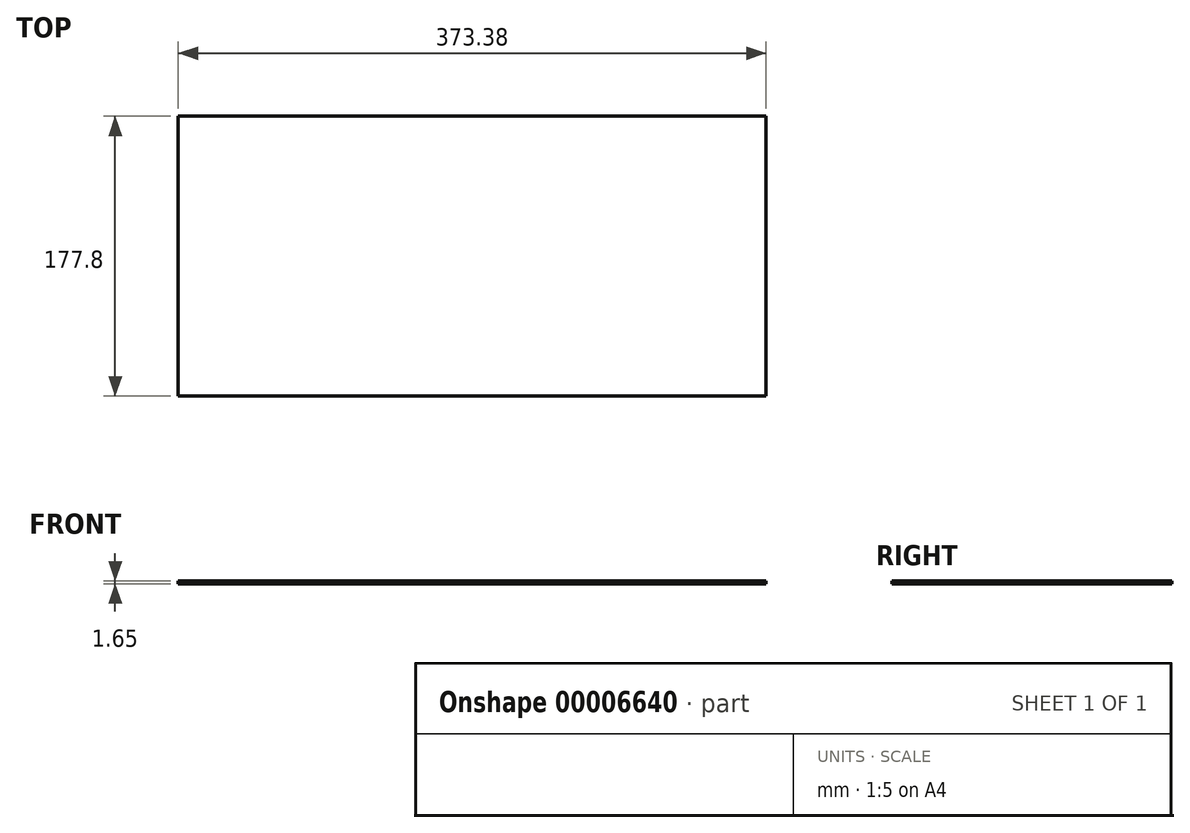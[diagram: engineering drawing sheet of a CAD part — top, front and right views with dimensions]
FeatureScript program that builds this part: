
annotation { "Feature Type Name" : "Feature", "Feature Type Description" : "" }
export const myFeature = defineFeature(function(context is Context, id is Id, definition is map)
    precondition{}
    {
        {
            var Q0;
            Q0=qCreatedBy(makeId("Top.planeOp"),FACE);
            var sketch = newSketch(context, id + "F0", { "sketchPlane" : qUnion([Q0])});
            skLineSegment(sketch, "E0.rect.bottom", {"start": v(186.69, 88.9) * mm, "end": v(-186.7, 88.9) * mm});
            skLineSegment(sketch, "E0.rect.top", {"start": v(186.7, -88.9) * mm, "end": v(-186.69, -88.9) * mm});
            skLineSegment(sketch, "E0.rect.left", {"start": v(186.69, 88.9) * mm, "end": v(186.7, -88.9) * mm});
            skLineSegment(sketch, "E0.rect.right", {"start": v(-186.7, 88.9) * mm, "end": v(-186.69, -88.9) * mm});
            skPoint(sketch, "E0.rect.middle", {"position": v(0, 0) * mm});
            skSolve(sketch);
        }
        {
            var Q0;
            Q0=makeQuery(id+"F0.imprint","IMPRINT",FACE,{"disambiguationData":[TD([[makeQuery(id+"F0.imprint","IMPRINT",EDGE,{"derivedFrom":sQuery(id+"F0.wireOp",EDGE,"E0.rect.bottom")}),1.0]])]});
            extrude(context, id + "F1", {"entities" : qUnion([Q0]), "depth" : 1.65 * mm});
        }
    });
